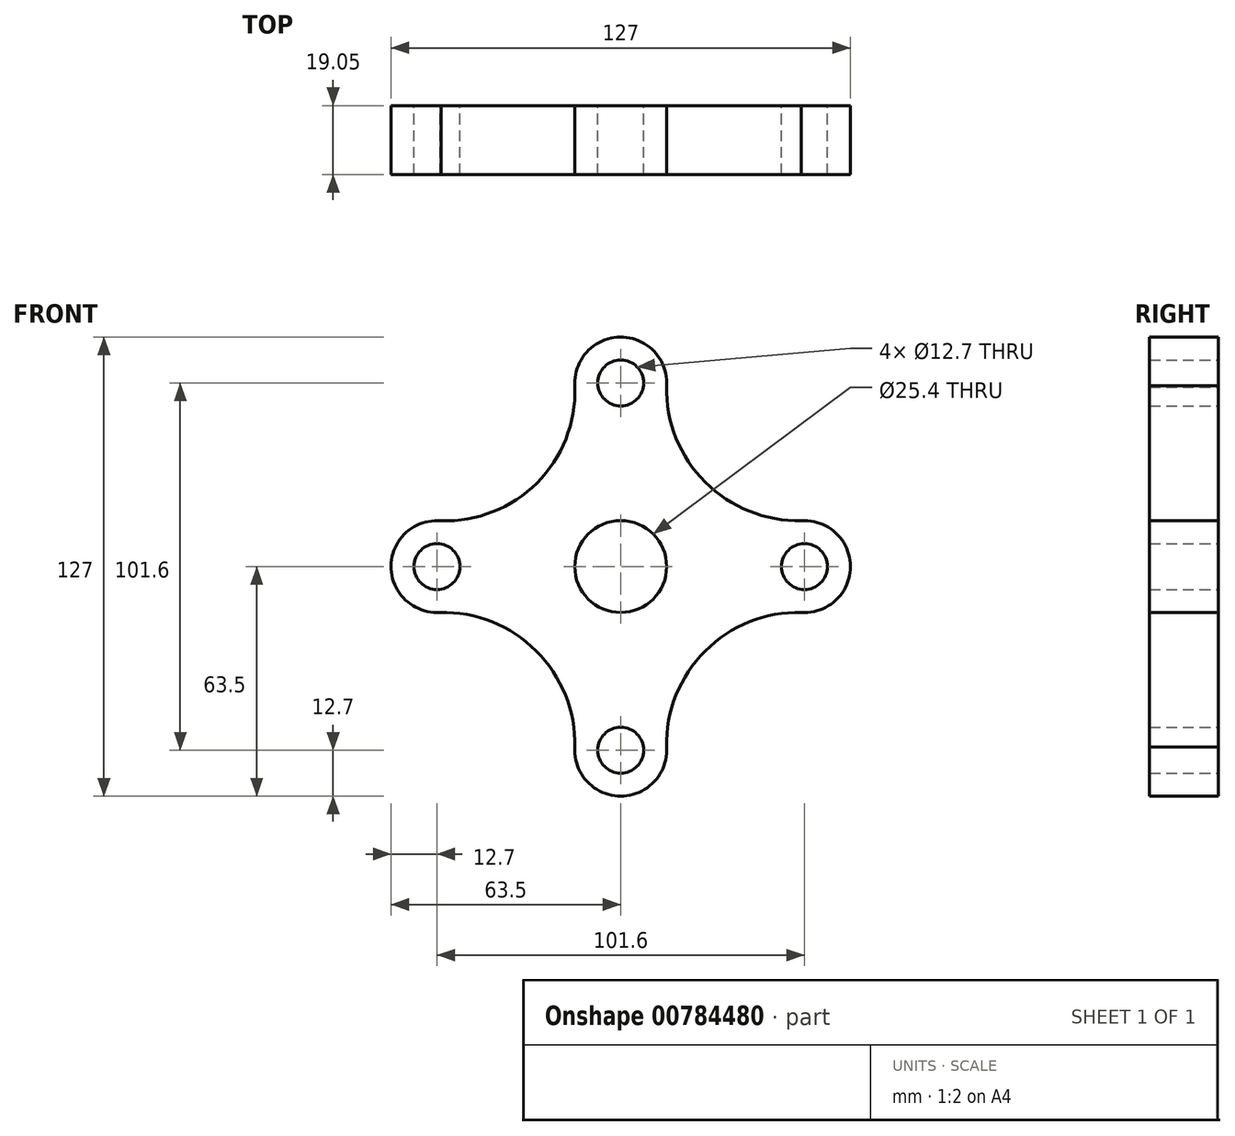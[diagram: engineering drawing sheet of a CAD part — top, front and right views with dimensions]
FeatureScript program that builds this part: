
annotation { "Feature Type Name" : "Feature", "Feature Type Description" : "" }
export const myFeature = defineFeature(function(context is Context, id is Id, definition is map)
    precondition{}
    {
        {
            var Q0;
            Q0=qCreatedBy(makeId("Front.planeOp"),FACE);
            var sketch = newSketch(context, id + "F0", { "sketchPlane" : qUnion([Q0])});
            skCircle(sketch, "E0", {"center": v(0, 0) * mm, "radius": 12.7 * mm});
            skCircle(sketch, "E1", {"center": v(0, 50.8) * mm, "radius": 6.35 * mm});
            skCircle(sketch, "E2.1.0", {"center": v(-50.8, 0) * mm, "radius": 6.35 * mm});
            skCircle(sketch, "E2.2.0", {"center": v(0, -50.8) * mm, "radius": 6.35 * mm});
            skCircle(sketch, "E2.3.0", {"center": v(50.8, 0) * mm, "radius": 6.35 * mm});
            skLineSegment(sketch, "E3", {"start": v(0, 50.8) * mm, "end": v(0, 63.5) * mm});
            skArc(sketch, "E4", {"start": v(12.67, 49.97) * mm, "mid": v(-0.16, 63.5) * mm, "end": v(-12.65, 49.65) * mm});
            skArc(sketch, "E5", {"start": v(-49.65, 12.65) * mm, "mid": v(-63.5, 0.16) * mm, "end": v(-49.97, -12.67) * mm});
            skArc(sketch, "E6", {"start": v(49.97, -12.67) * mm, "mid": v(63.5, 0) * mm, "end": v(49.97, 12.67) * mm});
            skArc(sketch, "E7", {"start": v(-12.67, -49.97) * mm, "mid": v(0, -63.5) * mm, "end": v(12.67, -49.97) * mm});
            skArc(sketch, "E8", {"start": v(-50.8, 12.7) * mm, "mid": v(-23.17, 23.17) * mm, "end": v(-12.7, 50.8) * mm});
            skArc(sketch, "E9", {"start": v(12.7, 50.8) * mm, "mid": v(23.36, 23.36) * mm, "end": v(50.8, 12.7) * mm});
            skArc(sketch, "E10", {"start": v(50.8, -12.7) * mm, "mid": v(23.36, -23.36) * mm, "end": v(12.7, -50.8) * mm});
            skArc(sketch, "E11", {"start": v(-12.7, -50.8) * mm, "mid": v(-23.36, -23.36) * mm, "end": v(-50.8, -12.7) * mm});
            skSolve(sketch);
        }
        {
            var Q0;
            Q0 = qSketchRegion(id + "F0", true);
            extrude(context, id + "F1", {"entities" : qUnion([Q0]), "depth" : 19.05 * mm, "offsetDistance" : 25.4 * mm});
        }
    });
